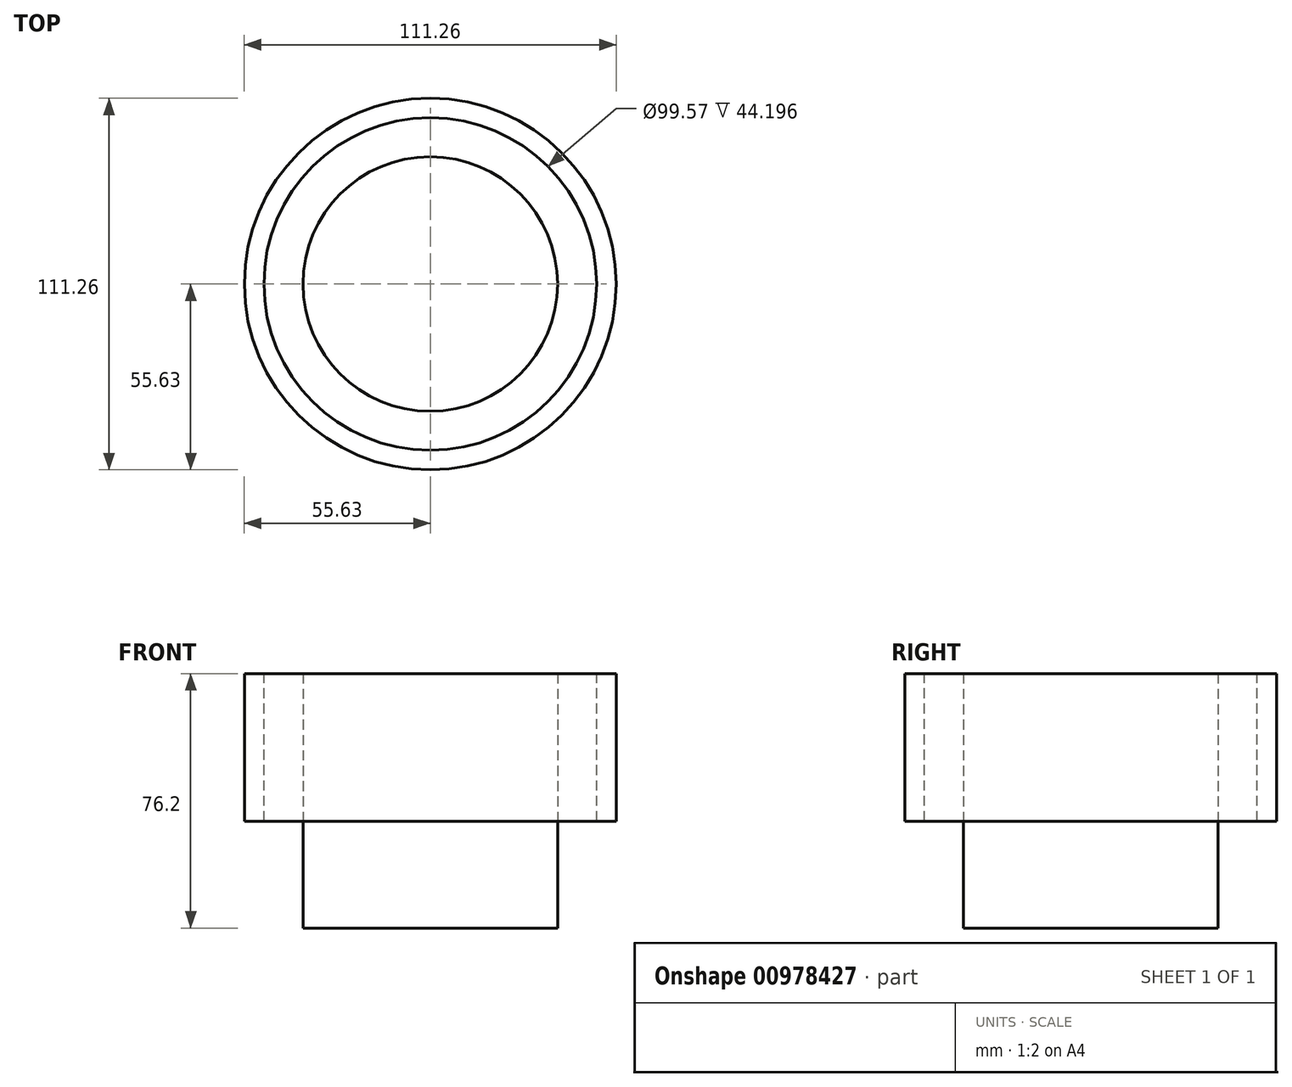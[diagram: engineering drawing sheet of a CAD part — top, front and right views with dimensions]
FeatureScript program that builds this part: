
annotation { "Feature Type Name" : "Feature", "Feature Type Description" : "" }
export const myFeature = defineFeature(function(context is Context, id is Id, definition is map)
    precondition{}
    {
        {
            var Q0;
            Q0=qCreatedBy(makeId("Top.planeOp"),FACE);
            var sketch = newSketch(context, id + "F0", { "sketchPlane" : qUnion([Q0])});
            skCircle(sketch, "E0", {"center": v(0, 0) * mm, "radius": 38.1 * mm});
            skSolve(sketch);
        }
        {
            var Q0;
            Q0 = qSketchRegion(id + "F0", true);
            extrude(context, id + "F1", {"entities" : qUnion([Q0]), "depth" : 76.2 * mm, "offsetDistance" : 25.4 * mm});
        }
        {
            var Q0;
            Q0=makeQuery(id+"F1.opExtrude","CAP_FACE",FACE,{"disambiguationData":[OSD([sQuery(id+"F0.wireOp",EDGE,"E0")])],"isStart":false});
            var sketch = newSketch(context, id + "F2", { "sketchPlane" : qUnion([Q0])});
            skCircle(sketch, "E1.0", {"center": v(0, 0) * mm, "radius": 55.63 * mm});
            skCircle(sketch, "E2.0", {"center": v(0, 0) * mm, "radius": 49.78 * mm});
            skSolve(sketch);
        }
        {
            var Q0;
            Q0=makeQuery(id+"F2.imprint","IMPRINT",FACE,{"disambiguationData":[TD([[makeQuery(id+"F2.imprint","IMPRINT",EDGE,{"derivedFrom":sQuery(id+"F2.wireOp",EDGE,"E1.0")}),1.0]])]});
            extrude(context, id + "F3", {"entities" : qUnion([Q0]), "oppositeDirection" : true, "depth" : 44.2 * mm, "offsetDistance" : 25.4 * mm});
        }
    });
